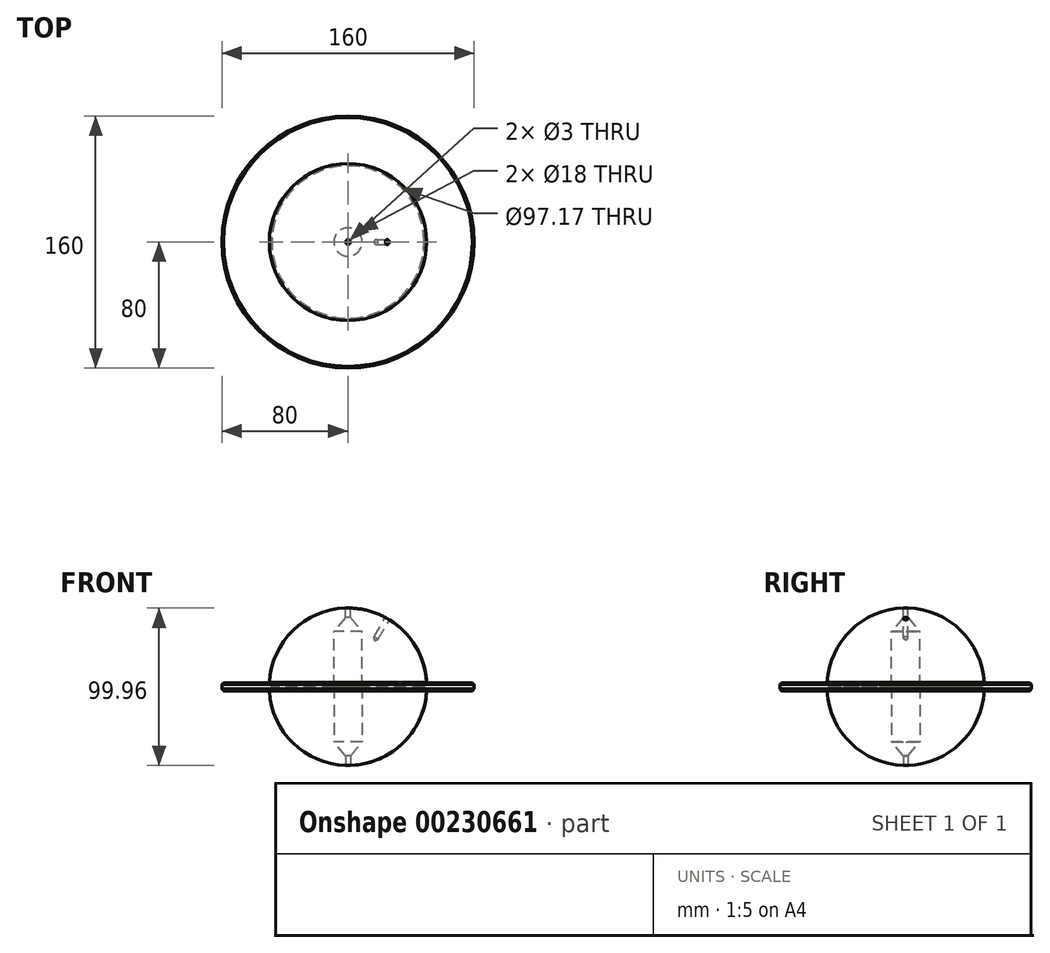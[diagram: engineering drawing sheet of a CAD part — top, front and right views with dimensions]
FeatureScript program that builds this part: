
annotation { "Feature Type Name" : "Feature", "Feature Type Description" : "" }
export const myFeature = defineFeature(function(context is Context, id is Id, definition is map)
    precondition{}
    {
        {
            var Q0;
            Q0=qCreatedBy(makeId("Front.planeOp"),FACE);
            var sketch = newSketch(context, id + "F0", { "sketchPlane" : qUnion([Q0])});
            skArc(sketch, "E0", {"start": v(50, 0) * mm, "mid": v(35.36, 35.36) * mm, "end": v(0, 50) * mm});
            skLineSegment(sketch, "E1", {"start": v(0, 50) * mm, "end": v(0, 0) * mm});
            skLineSegment(sketch, "E2", {"start": v(50, 0) * mm, "end": v(0, 0) * mm});
            skLineSegment(sketch, "E3", {"start": v(9, 0) * mm, "end": v(9, 35.04) * mm});
            skLineSegment(sketch, "E4", {"start": v(9, 35.04) * mm, "end": v(1.5, 43.98) * mm});
            skLineSegment(sketch, "E5", {"start": v(1.5, 43.98) * mm, "end": v(1.5, 49.98) * mm});
            skLineSegment(sketch, "E6", {"start": v(0, 0) * mm, "end": v(0, -22.04) * mm, "construction": true});
            skLineSegment(sketch, "E7", {"start": v(49.92, 2.79) * mm, "end": v(48.39, 1.5) * mm});
            skLineSegment(sketch, "E8", {"start": v(48.39, 1.5) * mm, "end": v(48.39, 0) * mm});
            skSolve(sketch);
        }
        {
            var Q0;
            {var subQ0=sQuery(id+"F0.wireOp",EDGE,"E3");Q0=makeQuery(id+"F0.imprint","IMPRINT",FACE,{"disambiguationData":[TD([[makeQuery(id+"F0.imprint","IMPRINT",EDGE,{"derivedFrom":subQ0}),-1.0]])]});}
            var Q1;
            Q1=sQuery(id+"F0.wireOp",EDGE,"E1");
            revolve(context, id + "F1", {"entities" : qUnion([Q0]), "axis" : qUnion([Q1]), "revolveType" : RevolveType.FULL});
        }
        {
            var Q0;
            Q0=makeQuery(id+"F1.opRevolve","SWEPT_BODY",BODY,{"disambiguationData":[OSD([sQuery(id+"F0.wireOp",EDGE,"E0"),sQuery(id+"F0.wireOp",EDGE,"E2"),sQuery(id+"F0.wireOp",EDGE,"E3"),sQuery(id+"F0.wireOp",EDGE,"E4"),sQuery(id+"F0.wireOp",EDGE,"E5"),sQuery(id+"F0.wireOp",EDGE,"E7"),sQuery(id+"F0.wireOp",EDGE,"E8")])]});
            var Q1;
            Q1=qCreatedBy(makeId("Top.planeOp"),FACE);
            mirror(context, id + "F2", {"entities" : qUnion([Q0]), "mirrorPlane" : qUnion([Q1])});
        }
        {
            var Q0;
            Q0=qCreatedBy(makeId("Front.planeOp"),FACE);
            var sketch = newSketch(context, id + "F3", { "sketchPlane" : qUnion([Q0])});
            skLineSegment(sketch, "E9", {"start": v(49.73, 2.5) * mm, "end": v(80, 2.5) * mm});
            skLineSegment(sketch, "E10", {"start": v(80, 2.5) * mm, "end": v(80, -2.5) * mm});
            skLineSegment(sketch, "E11", {"start": v(80, -2.5) * mm, "end": v(49.73, -2.5) * mm});
            skLineSegment(sketch, "E12", {"start": v(49.73, -2.5) * mm, "end": v(48.59, -1.54) * mm});
            skLineSegment(sketch, "E13", {"start": v(48.59, -1.54) * mm, "end": v(48.59, 1.54) * mm});
            skLineSegment(sketch, "E14", {"start": v(48.59, 1.54) * mm, "end": v(49.73, 2.5) * mm});
            skLineSegment(sketch, "E15", {"start": v(65.88, 0) * mm, "end": v(86.68, 0) * mm, "construction": true});
            skLineSegment(sketch, "E16", {"start": v(0, 0) * mm, "end": v(0, -21.23) * mm, "construction": true});
            skPoint(sketch, "E17", {"position": v(80, 0) * mm});
            skPoint(sketch, "E18", {"position": v(48.59, 0) * mm});
            skLineSegment(sketch, "E19.0", {"start": v(49.92, 2.79) * mm, "end": v(48.39, 1.5) * mm});
            skLineSegment(sketch, "E20", {"start": v(48.39, -1.5) * mm, "end": v(49.92, -2.79) * mm});
            skLineSegment(sketch, "E21", {"start": v(48.39, 0) * mm, "end": v(48.39, -1.5) * mm});
            skSolve(sketch);
        }
        {
            var Q0;
            Q0=makeQuery(id+"F3.imprint","IMPRINT",FACE,{"disambiguationData":[TD([[makeQuery(id+"F3.imprint","IMPRINT",EDGE,{"derivedFrom":sQuery(id+"F3.wireOp",EDGE,"E9")}),-1.0]])]});
            var Q1;
            Q1=sQuery(id+"F3.wireOp",EDGE,"E16");
            revolve(context, id + "F4", {"entities" : qUnion([Q0]), "axis" : qUnion([Q1]), "revolveType" : RevolveType.FULL});
        }
        {
            var Q0;
            Q0=qCreatedBy(makeId("Front.planeOp"),FACE);
            var sketch = newSketch(context, id + "F5", { "sketchPlane" : qUnion([Q0])});
            skLineSegment(sketch, "E22", {"start": v(0, 0) * mm, "end": v(30.06, 52.07) * mm});
            skLineSegment(sketch, "E23", {"start": v(16.97, 29.4) * mm, "end": v(19.17, 30.2) * mm});
            skLineSegment(sketch, "E24", {"start": v(19.17, 30.2) * mm, "end": v(26.77, 43.37) * mm});
            skLineSegment(sketch, "E25", {"start": v(26.77, 43.37) * mm, "end": v(25.47, 44.12) * mm});
            skSolve(sketch);
        }
        {
            var Q0;
            {var subQ0=sQuery(id+"F5.wireOp",EDGE,"E23");Q0=makeQuery(id+"F5.imprint","IMPRINT",FACE,{"disambiguationData":[TD([[makeQuery(id+"F5.imprint","IMPRINT",EDGE,{"derivedFrom":subQ0}),1.0]])]});}
            var Q1;
            Q1=sQuery(id+"F5.wireOp",EDGE,"E22");
            revolve(context, id + "F6", {"operationType" : NewBodyOperationType.REMOVE, "entities" : qUnion([Q0]), "axis" : qUnion([Q1]), "revolveType" : RevolveType.FULL, "oppositeDirection" : true});
        }
        {
            var Q0;
            Q0=makeQuery(id+"F4.opRevolve","SWEPT_EDGE",EDGE,{"disambiguationData":[OSD([sQuery(id+"F3.wireOp",EDGE,"E9"),sQuery(id+"F3.wireOp",EDGE,"E10")])]});
            var Q1;
            Q1=makeQuery(id+"F4.opRevolve","SWEPT_EDGE",EDGE,{"disambiguationData":[OSD([sQuery(id+"F3.wireOp",EDGE,"E10"),sQuery(id+"F3.wireOp",EDGE,"E11")])]});
            chamfer(context, id + "F7", {"entities" : qUnion([Q0, Q1]), "width" : 1 * mm, "tangentPropagation" : true});
        }
    });
